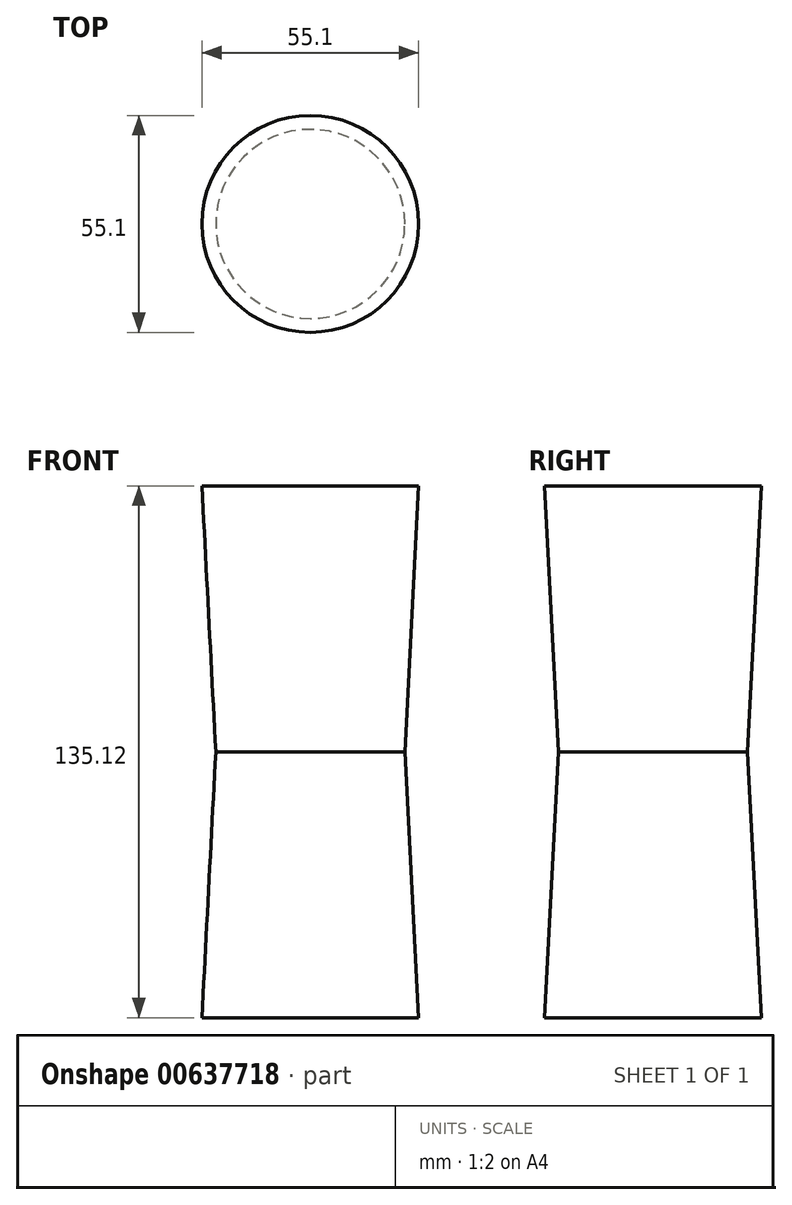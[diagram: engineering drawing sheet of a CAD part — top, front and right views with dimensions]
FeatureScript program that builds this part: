
annotation { "Feature Type Name" : "Feature", "Feature Type Description" : "" }
export const myFeature = defineFeature(function(context is Context, id is Id, definition is map)
    precondition{}
    {
        {
            var Q0;
            Q0=qCreatedBy(makeId("Top.planeOp"),FACE);
            var sketch = newSketch(context, id + "F0", { "sketchPlane" : qUnion([Q0])});
            skCircle(sketch, "E0", {"center": v(0, 0) * mm, "radius": 24 * mm});
            skSolve(sketch);
        }
        {
            var Q0;
            Q0 = qSketchRegion(id + "F0", true);
            extrude(context, id + "F1", {"entities" : qUnion([Q0]), "oppositeDirection" : true, "depth" : 67.56 * mm, "offsetDistance" : 25.4 * mm, "hasDraft" : true, "draftAngle" : 3 * degree, "hasSecondDirection" : true, "secondDirectionOppositeDirection" : false, "secondDirectionDepth" : 67.56 * mm, "hasSecondDirectionDraft" : true, "secondDirectionDraftAngle" : 3 * degree});
        }
    });
